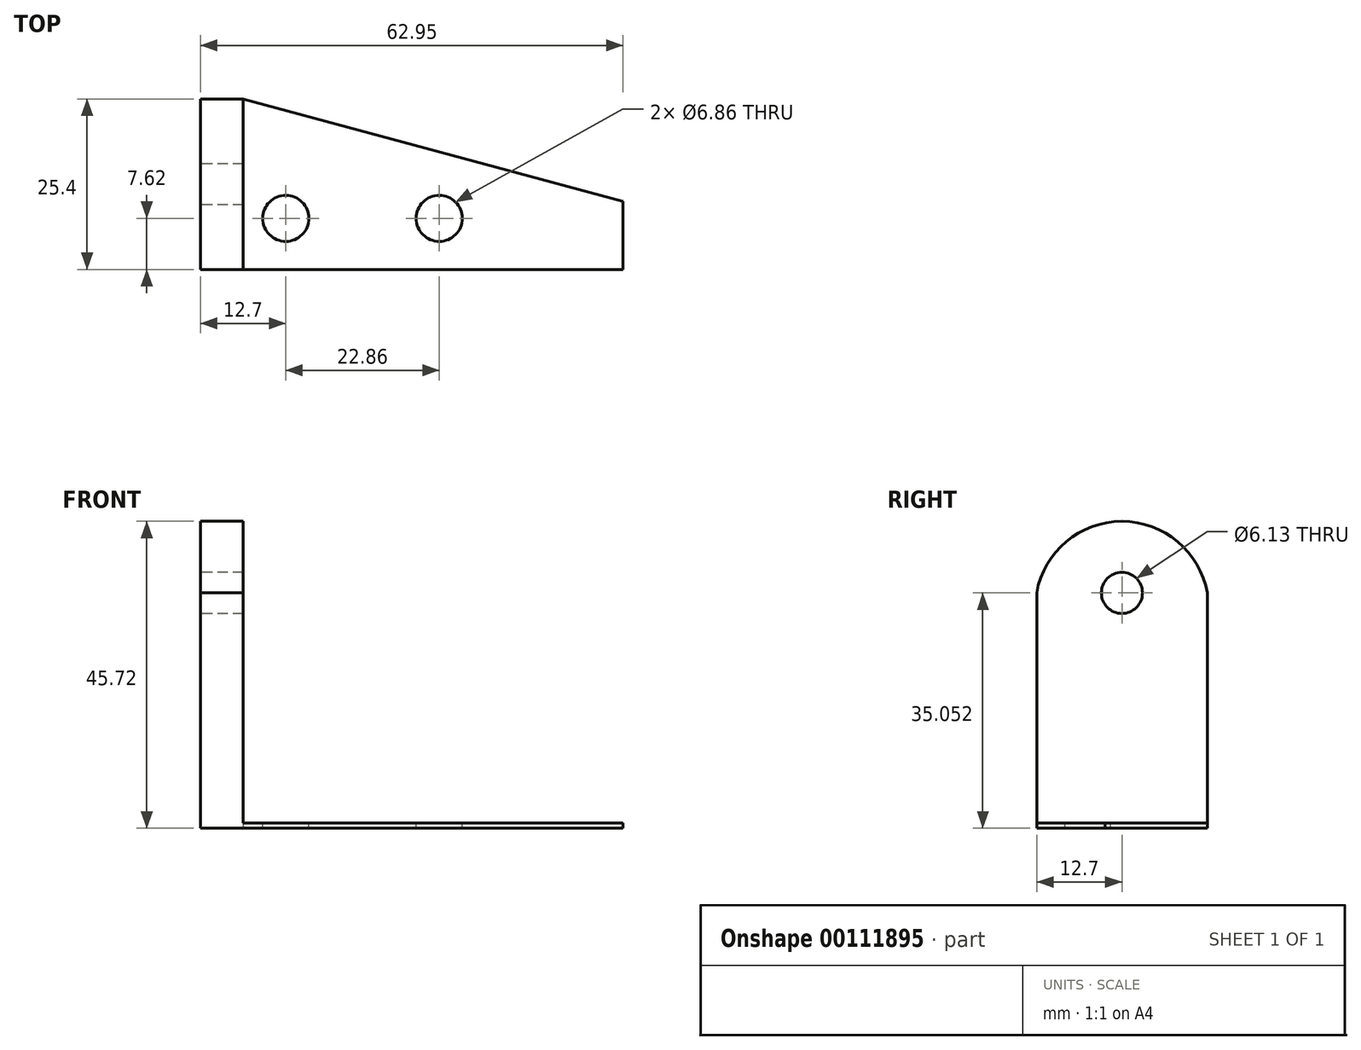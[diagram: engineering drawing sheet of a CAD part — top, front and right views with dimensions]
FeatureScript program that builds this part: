
annotation { "Feature Type Name" : "Feature", "Feature Type Description" : "" }
export const myFeature = defineFeature(function(context is Context, id is Id, definition is map)
    precondition{}
    {
        {
            var Q0;
            Q0=qCreatedBy(makeId("Top.planeOp"),FACE);
            var sketch = newSketch(context, id + "F0", { "sketchPlane" : qUnion([Q0])});
            skLineSegment(sketch, "E0", {"start": v(0, 0) * mm, "end": v(0, -25.4) * mm});
            skLineSegment(sketch, "E1", {"start": v(0, -25.4) * mm, "end": v(62.95, -25.4) * mm});
            skPoint(sketch, "E2.end.orphan", {"position": v(97.55, -22.7) * mm});
            skLineSegment(sketch, "E3", {"start": v(6.35, 0) * mm, "end": v(6.35, -25.4) * mm});
            skLineSegment(sketch, "E4", {"start": v(6.35, -25.4) * mm, "end": v(0, -25.4) * mm});
            skLineSegment(sketch, "E5", {"start": v(0, 0) * mm, "end": v(6.35, 0) * mm});
            skLineSegment(sketch, "E6", {"start": v(6.35, 0) * mm, "end": v(62.95, -15.24) * mm});
            skLineSegment(sketch, "E7", {"start": v(62.95, -15.24) * mm, "end": v(62.95, -25.4) * mm});
            skPoint(sketch, "E8.start.orphan", {"position": v(0, 38.1) * mm});
            skPoint(sketch, "E9.orphan", {"position": v(97.55, 0) * mm});
            skPoint(sketch, "E10.end.orphan", {"position": v(97.55, -25.4) * mm});
            skSolve(sketch);
        }
        {
            var Q0;
            Q0=makeQuery(id+"F0.imprint","IMPRINT",FACE,{"disambiguationData":[TD([[makeQuery(id+"F0.imprint","IMPRINT",EDGE,{"derivedFrom":sQuery(id+"F0.wireOp",EDGE,"E0")}),1.0]])]});
            extrude(context, id + "F1", {"entities" : qUnion([Q0]), "depth" : 45.72 * mm});
        }
        {
            var Q0;
            Q0=makeQuery(id+"F1.opExtrude","SWEPT_FACE",FACE,{"disambiguationData":[OSD([sQuery(id+"F0.wireOp",EDGE,"E0")])]});
            var sketch = newSketch(context, id + "F2", { "sketchPlane" : qUnion([Q0])});
            skCircle(sketch, "E11", {"center": v(12.7, 35.05) * mm, "radius": 3.06 * mm});
            skSolve(sketch);
        }
        {
            var Q0;
            Q0=makeQuery(id+"F2.imprint","IMPRINT",FACE,{"disambiguationData":[TD([[makeQuery(id+"F2.imprint","IMPRINT",EDGE,{"derivedFrom":sQuery(id+"F2.wireOp",EDGE,"E11")}),1.0]])]});
            var Q1;
            Q1=sQuery(id+"F2.wireOp",EDGE,"E11");
            extrude(context, id + "F3", {"entities" : qUnion([Q0]), "operationType" : NewBodyOperationType.REMOVE, "surfaceEntities" : qUnion([Q1]), "oppositeDirection" : true, "depth" : 25.4 * mm});
        }
        {
            var Q0;
            Q0=makeQuery(id+"F1.opExtrude","SWEPT_FACE",FACE,{"disambiguationData":[OSD([sQuery(id+"F0.wireOp",EDGE,"E0")])]});
            var sketch = newSketch(context, id + "F4", { "sketchPlane" : qUnion([Q0])});
            skPoint(sketch, "E12", {"position": v(12.7, 35.05) * mm});
            skLineSegment(sketch, "E13", {"start": v(0, 35.05) * mm, "end": v(0, 35.05) * mm});
            skArc(sketch, "E14", {"start": v(25.4, 35.05) * mm, "mid": v(12.7, 45.72) * mm, "end": v(0, 35.05) * mm});
            skSolve(sketch);
        }
        {
            var Q0;
            Q0 = qSketchRegion(id + "F0", true);
            extrude(context, id + "F5", {"entities" : qUnion([Q0]), "operationType" : NewBodyOperationType.ADD, "depth" : 0.76 * mm});
        }
        {
            var Q0;
            Q0 = qSketchRegion(id + "F4", true);
            var Q1;
            {var subQ0=sQuery(id+"F4.wireOp",EDGE,"E14");var subQ1=sQuery(id+"F0.wireOp",EDGE,"E0");var subQ4=makeQuery(id+"F1.opExtrude","CAP_EDGE",EDGE,{"disambiguationData":[OSD([subQ1])],"isStart":false});var subQ5=makeQuery(id+"F4.imprint","INTERSECT",VERTEX,{"derivedFrom":[subQ4,subQ0]});Q1=makeQuery(id+"F4.imprint","IMPRINT",FACE,{"disambiguationData":[TD([[makeQuery(id+"F4.imprint","IMPRINT",EDGE,{"disambiguationData":[TD([[subQ5,-1.0]])],"derivedFrom":subQ0}),-1.0]])]});}
            var Q2;
            {var subQ0=sQuery(id+"F4.wireOp",EDGE,"E14");var subQ1=sQuery(id+"F0.wireOp",EDGE,"E0");var subQ4=makeQuery(id+"F1.opExtrude","CAP_EDGE",EDGE,{"disambiguationData":[OSD([subQ1])],"isStart":false});var subQ5=makeQuery(id+"F4.imprint","INTERSECT",VERTEX,{"derivedFrom":[subQ4,subQ0]});Q2=makeQuery(id+"F4.imprint","IMPRINT",FACE,{"disambiguationData":[TD([[makeQuery(id+"F4.imprint","IMPRINT",EDGE,{"disambiguationData":[TD([[subQ5,1.0]])],"derivedFrom":subQ0}),-1.0]])]});}
            extrude(context, id + "F6", {"entities" : qUnion([Q0, Q1, Q2]), "operationType" : NewBodyOperationType.REMOVE, "oppositeDirection" : true, "depth" : 25.4 * mm});
        }
        {
            var Q0;
            Q0=makeQuery(id+"F5.opExtrude","CAP_FACE",FACE,{"disambiguationData":[OSD([sQuery(id+"F0.wireOp",EDGE,"E0"),sQuery(id+"F0.wireOp",EDGE,"E1"),sQuery(id+"F0.wireOp",EDGE,"E10"),sQuery(id+"F0.wireOp",EDGE,"E8"),sQuery(id+"F0.wireOp",EDGE,"E4"),sQuery(id+"F0.wireOp",EDGE,"bIw8MrPn-ra0x-hvnV-qSvT-B4FSMQPOL9A2")])],"isStart":false});
            var sketch = newSketch(context, id + "F7", { "sketchPlane" : qUnion([Q0])});
            skCircle(sketch, "E15", {"center": v(12.7, -17.78) * mm, "radius": 3.43 * mm});
            skCircle(sketch, "E16", {"center": v(35.56, -17.78) * mm, "radius": 3.43 * mm});
            skSolve(sketch);
        }
        {
            var Q0;
            Q0=makeQuery(id+"F7.imprint","IMPRINT",FACE,{"disambiguationData":[TD([[makeQuery(id+"F7.imprint","IMPRINT",EDGE,{"derivedFrom":sQuery(id+"F7.wireOp",EDGE,"E15")}),1.0]])]});
            var Q1;
            Q1=makeQuery(id+"F7.imprint","IMPRINT",FACE,{"disambiguationData":[TD([[makeQuery(id+"F7.imprint","IMPRINT",EDGE,{"derivedFrom":sQuery(id+"F7.wireOp",EDGE,"E16")}),1.0]])]});
            extrude(context, id + "F8", {"entities" : qUnion([Q0, Q1]), "operationType" : NewBodyOperationType.REMOVE, "oppositeDirection" : true, "depth" : 25.4 * mm});
        }
    });
